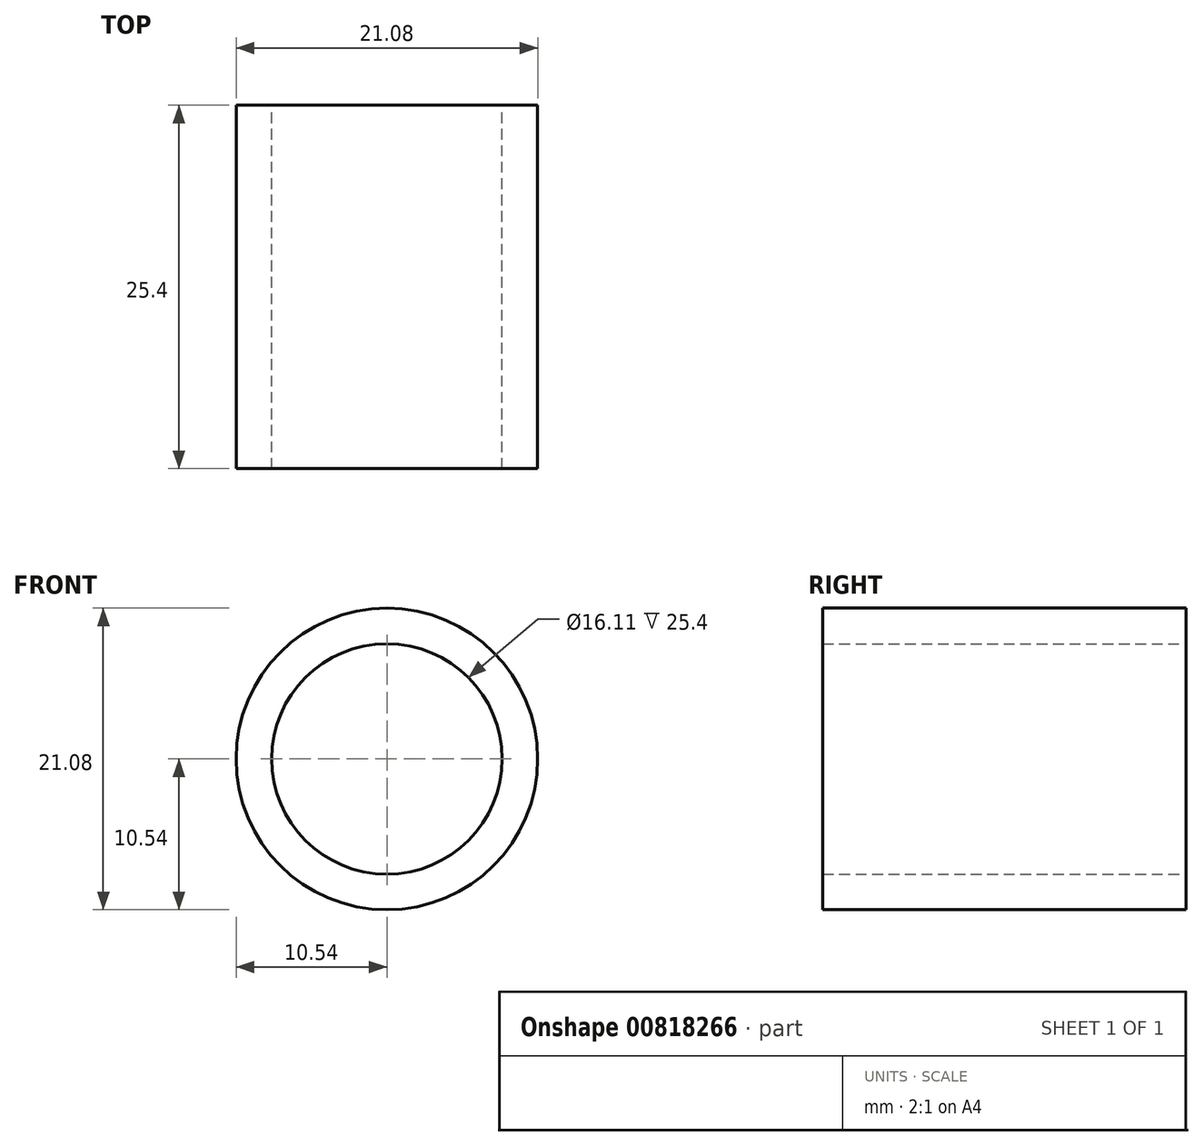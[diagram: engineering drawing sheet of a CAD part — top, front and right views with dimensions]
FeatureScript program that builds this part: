
annotation { "Feature Type Name" : "Feature", "Feature Type Description" : "" }
export const myFeature = defineFeature(function(context is Context, id is Id, definition is map)
    precondition{}
    {
        {
            var Q0;
            Q0=qCreatedBy(makeId("Front.planeOp"),FACE);
            var sketch = newSketch(context, id + "F0", { "sketchPlane" : qUnion([Q0])});
            skCircle(sketch, "E0", {"center": v(0, 0) * mm, "radius": 8.06 * mm});
            skCircle(sketch, "E1", {"center": v(0, 0) * mm, "radius": 10.54 * mm});
            skSolve(sketch);
        }
        {
            var Q0;
            Q0=makeQuery(id+"F0.imprint","IMPRINT",FACE,{"disambiguationData":[TD([[makeQuery(id+"F0.imprint","IMPRINT",EDGE,{"derivedFrom":sQuery(id+"F0.wireOp",EDGE,"E0")}),-1.0]])]});
            extrude(context, id + "F1", {"entities" : qUnion([Q0]), "depth" : 25.4 * mm, "offsetDistance" : 25.4 * mm});
        }
    });
